# Revit family: 54L
name_source: partatom
category: Lighting Fixtures
revit_build: Autodesk Revit 2013 (Build: 20120221_2030(x64)
units: mm (PartAtom-declared; Revit-internal decimal feet)

## types (5) — shared parameters
Apparent Load = 4 VA
Assembly Code = D5020210
Color Filter = 16777215
Description = Arcos Wall LED
Dimming Lamp Color Temperature Shift = <None>
Emit Shape Visible in Rendering = No
Emit from Rectangle Width = 2"
Fixture distribution = Asymmetric Indirect
Lamp = LED
Load Classification = Lighting
Manufacturer = LiteControl
Manufacturer Fax = 781 293 2849
Model = 54L W
Mounting = Wall-Mounted
Photometric Web File = generic
Power Factor = 1
Product Documentation Link = http://cdn.litecontrol.com
Product Material = Paint - Hubbell - Matte White
Product Page URL = http://www.litecontrol.com
Reflector Finish = Hubbell - White Glass
Tilt Angle = -90.00°
URL = http://www.litecontrol.com
Watts = 4 W

## per-type parameters (varying)
| type | Emit from Rectangle Length | Length |
| 54L-W-02 | 22" | 24" |
| 54L-W-03 | 34" | 36" |
| 54L-W-04 | 46" | 48" |
| 54L-W-06 | 70" | 72" |
| 54L-W-08 | 94" | 96" |

## geometry (parser evidence)
native form markers: Blend x15, Sweep x1
no freeform markers — native parametric forms only
